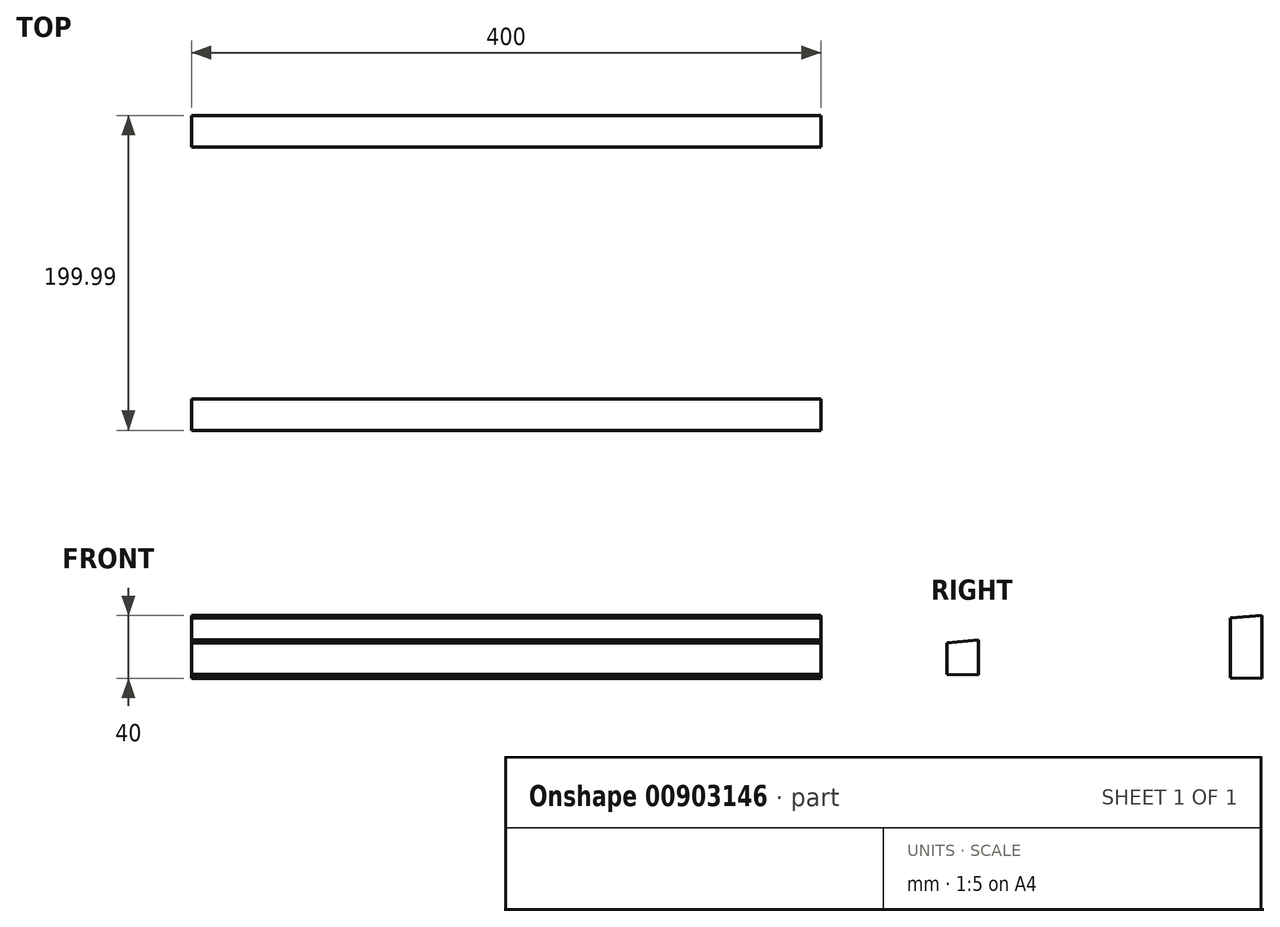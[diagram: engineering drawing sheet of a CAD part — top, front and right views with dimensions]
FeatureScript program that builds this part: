
annotation { "Feature Type Name" : "Feature", "Feature Type Description" : "" }
export const myFeature = defineFeature(function(context is Context, id is Id, definition is map)
    precondition{}
    {
        {
            var Q0;
            Q0=qCreatedBy(makeId("Right.planeOp"),FACE);
            var sketch = newSketch(context, id + "F0", { "sketchPlane" : qUnion([Q0])});
            skLineSegment(sketch, "E0", {"start": v(-101.35, 10.02) * mm, "end": v(-101.35, -9.98) * mm});
            skLineSegment(sketch, "E1", {"start": v(98.64, 27.51) * mm, "end": v(98.64, -12.49) * mm});
            skLineSegment(sketch, "E2", {"start": v(98.64, -12.49) * mm, "end": v(88.64, -12.36) * mm, "construction": true});
            skLineSegment(sketch, "E3", {"start": v(98.64, 27.51) * mm, "end": v(88.64, 26.64) * mm, "construction": true});
            skLineSegment(sketch, "E4", {"start": v(88.64, -12.36) * mm, "end": v(98.64, -12.49) * mm, "construction": true});
            skLineSegment(sketch, "E5", {"start": v(88.64, 26.64) * mm, "end": v(98.64, 27.51) * mm});
            skLineSegment(sketch, "E6", {"start": v(98.64, -12.49) * mm, "end": v(88.64, -12.36) * mm});
            skLineSegment(sketch, "E7", {"start": v(-81.35, -10.23) * mm, "end": v(-81.35, 11.77) * mm});
            skLineSegment(sketch, "E8.trimOffspring", {"start": v(-81.35, 11.77) * mm, "end": v(98.64, 27.51) * mm, "construction": true});
            skLineSegment(sketch, "E9.trimOffspring", {"start": v(-81.35, -10.23) * mm, "end": v(98.64, -12.49) * mm, "construction": true});
            skLineSegment(sketch, "E10", {"start": v(-101.35, 10.02) * mm, "end": v(-81.35, 11.77) * mm});
            skLineSegment(sketch, "E11", {"start": v(-81.35, -10.23) * mm, "end": v(-101.35, -9.98) * mm});
            skLineSegment(sketch, "E12", {"start": v(88.64, -12.36) * mm, "end": v(78.64, -12.24) * mm});
            skLineSegment(sketch, "E13", {"start": v(78.64, -12.24) * mm, "end": v(78.64, 25.76) * mm});
            skLineSegment(sketch, "E14", {"start": v(88.64, 26.64) * mm, "end": v(78.64, 25.76) * mm});
            skSolve(sketch);
        }
        {
            var Q0;
            Q0=makeQuery(id+"F0.imprint","IMPRINT",FACE,{"disambiguationData":[TD([[makeQuery(id+"F0.imprint","IMPRINT",EDGE,{"derivedFrom":sQuery(id+"F0.wireOp",EDGE,"E0")}),1.0]])]});
            var Q1;
            Q1=makeQuery(id+"F0.imprint","IMPRINT",FACE,{"disambiguationData":[TD([[makeQuery(id+"F0.imprint","IMPRINT",EDGE,{"derivedFrom":sQuery(id+"F0.wireOp",EDGE,"E1")}),-1.0]])]});
            extrude(context, id + "F1", {"entities" : qUnion([Q0, Q1]), "depth" : 400 * mm, "offsetDistance" : 25 * mm});
        }
    });
